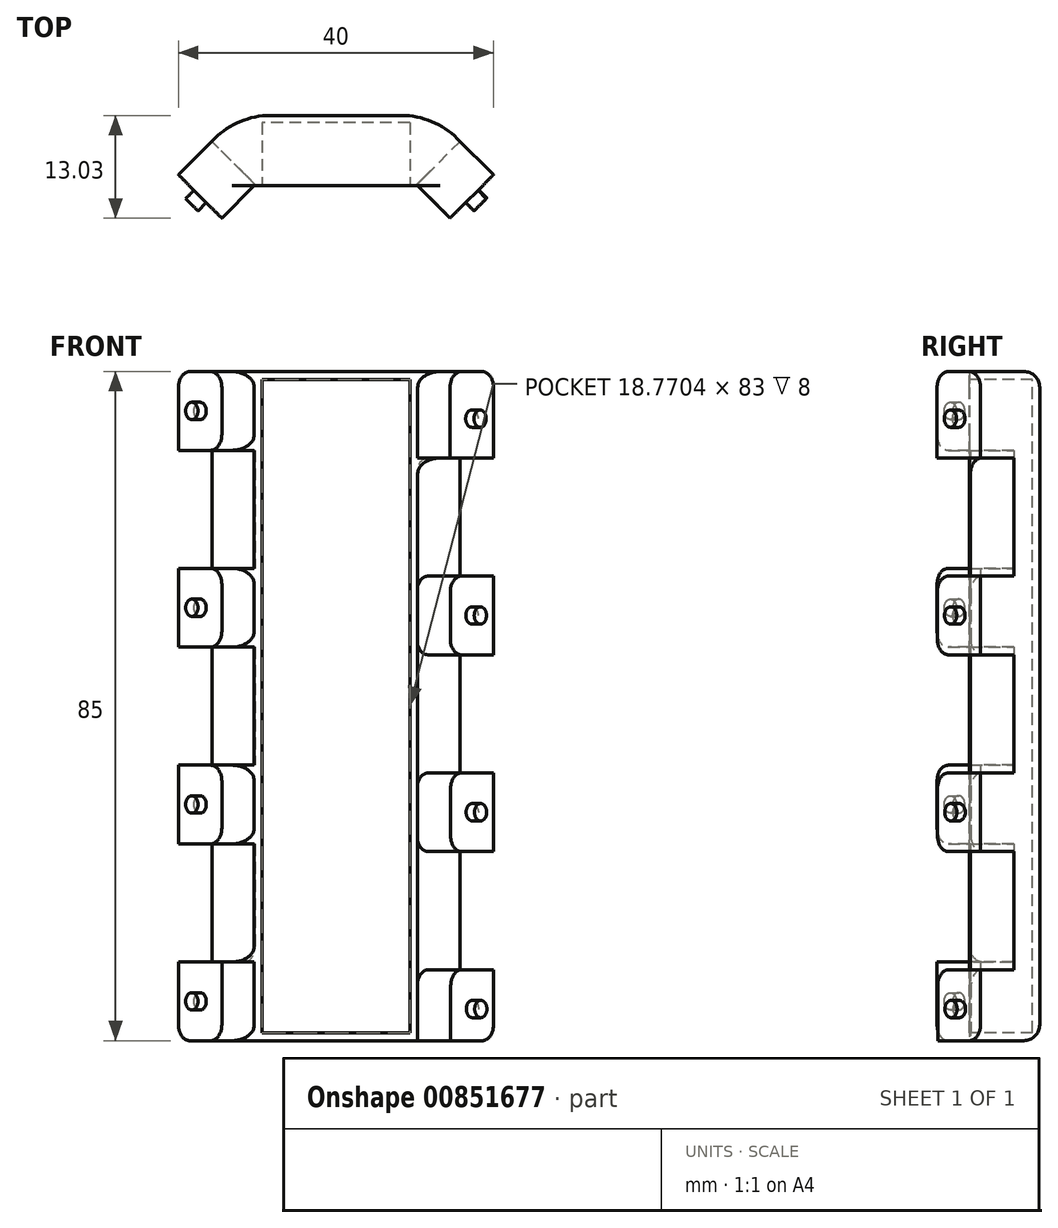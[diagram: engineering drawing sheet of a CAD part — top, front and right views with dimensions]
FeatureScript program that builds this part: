
annotation { "Feature Type Name" : "Feature", "Feature Type Description" : "" }
export const myFeature = defineFeature(function(context is Context, id is Id, definition is map)
    precondition{}
    {
        {
            var Q0;
            Q0=qCreatedBy(makeId("Top.planeOp"),FACE);
            var sketch = newSketch(context, id + "F0", { "sketchPlane" : qUnion([Q0])});
            skLineSegment(sketch, "E0", {"start": v(0, 0) * mm, "end": v(56.57, 56.57) * mm, "construction": true});
            skLineSegment(sketch, "E1", {"start": v(0, 0) * mm, "end": v(-56.57, 56.57) * mm, "construction": true});
            skLineSegment(sketch, "E2", {"start": v(0, 0) * mm, "end": v(14.5, 0) * mm});
            skLineSegment(sketch, "E3", {"start": v(0, 0) * mm, "end": v(-14.5, 0) * mm});
            skLineSegment(sketch, "E4", {"start": v(-14.5, -5.83) * mm, "end": v(-14.5, 16.54) * mm, "construction": true});
            skLineSegment(sketch, "E5", {"start": v(14.5, -3.6) * mm, "end": v(14.5, 17.08) * mm, "construction": true});
            skLineSegment(sketch, "E6", {"start": v(0, 0) * mm, "end": v(-20, 0) * mm, "construction": true});
            skLineSegment(sketch, "E7", {"start": v(0, 0) * mm, "end": v(20, 0) * mm, "construction": true});
            skLineSegment(sketch, "E8", {"start": v(-20, 0) * mm, "end": v(-20, 20) * mm, "construction": true});
            skLineSegment(sketch, "E9", {"start": v(20, 0) * mm, "end": v(20, 20) * mm, "construction": true});
            skLineSegment(sketch, "E10", {"start": v(-14.5, 14.5) * mm, "end": v(-10.39, 18.61) * mm});
            skLineSegment(sketch, "E11", {"start": v(-10.39, 18.61) * mm, "end": v(0, 18.61) * mm});
            skLineSegment(sketch, "E12", {"start": v(-20, 20) * mm, "end": v(-12.47, 27.53) * mm});
            skLineSegment(sketch, "E13", {"start": v(-12.47, 27.53) * mm, "end": v(0, 27.53) * mm});
            skLineSegment(sketch, "E14.MirrorCS", {"start": v(12.47, 27.53) * mm, "end": v(0, 27.53) * mm});
            skLineSegment(sketch, "E15.MirrorCS", {"start": v(20, 20) * mm, "end": v(12.47, 27.53) * mm});
            skLineSegment(sketch, "E16.MirrorCS", {"start": v(14.5, 14.5) * mm, "end": v(10.39, 18.61) * mm});
            skLineSegment(sketch, "E17.MirrorCS", {"start": v(10.39, 18.61) * mm, "end": v(0, 18.61) * mm});
            skLineSegment(sketch, "E18", {"start": v(-20, 20) * mm, "end": v(-14.5, 14.5) * mm});
            skLineSegment(sketch, "E19", {"start": v(14.5, 14.5) * mm, "end": v(20, 20) * mm});
            skSolve(sketch);
        }
        {
            var Q0;
            Q0=makeQuery(id+"F0.imprint","IMPRINT",FACE,{"disambiguationData":[TD([[makeQuery(id+"F0.imprint","IMPRINT",EDGE,{"derivedFrom":sQuery(id+"F0.wireOp",EDGE,"E10")}),1.0]])]});
            extrude(context, id + "F1", {"entities" : qUnion([Q0]), "depth" : 85 * mm, "offsetDistance" : 25 * mm});
        }
        {
            var Q0;
            Q0=makeQuery(id+"F1.opExtrude","SWEPT_EDGE",EDGE,{"disambiguationData":[OSD([sQuery(id+"F0.wireOp",EDGE,"E12"),sQuery(id+"F0.wireOp",EDGE,"E13")])]});
            var Q1;
            Q1=makeQuery(id+"F1.opExtrude","SWEPT_EDGE",EDGE,{"disambiguationData":[OSD([sQuery(id+"F0.wireOp",EDGE,"E14.MirrorCS"),sQuery(id+"F0.wireOp",EDGE,"E15.MirrorCS")])]});
            fillet(context, id + "F2", {"entities" : qUnion([Q0, Q1]), "radius" : 10 * mm, "tangentPropagation" : true, "allowEdgeOverflow" : false});
        }
        {
            var Q0;
            Q0=makeQuery(id+"F1.opExtrude","SWEPT_FACE",FACE,{"disambiguationData":[OSD([sQuery(id+"F0.wireOp",EDGE,"E19")])]});
            var sketch = newSketch(context, id + "F3", { "sketchPlane" : qUnion([Q0])});
            skLineSegment(sketch, "E20.bottom", {"start": v(28.28, 84.02) * mm, "end": v(20.5, 84.02) * mm});
            skLineSegment(sketch, "E20.top", {"start": v(28.28, 74.02) * mm, "end": v(20.5, 74.02) * mm});
            skLineSegment(sketch, "E20.left", {"start": v(28.28, 84.02) * mm, "end": v(28.28, 74.02) * mm});
            skLineSegment(sketch, "E20.right", {"start": v(20.5, 84.02) * mm, "end": v(20.5, 74.02) * mm});
            skLineSegment(sketch, "E21.0.1.0", {"start": v(28.32, 59.02) * mm, "end": v(28.32, 49.02) * mm});
            skLineSegment(sketch, "E21.0.1.1", {"start": v(28.32, 59.02) * mm, "end": v(20.54, 59.02) * mm});
            skLineSegment(sketch, "E21.0.1.2", {"start": v(20.54, 59.02) * mm, "end": v(20.54, 49.02) * mm});
            skLineSegment(sketch, "E21.0.1.3", {"start": v(28.32, 49.02) * mm, "end": v(20.54, 49.02) * mm});
            skLineSegment(sketch, "E21.0.2.0", {"start": v(28.36, 34.02) * mm, "end": v(28.36, 24.02) * mm});
            skLineSegment(sketch, "E21.0.2.1", {"start": v(28.36, 34.02) * mm, "end": v(20.58, 34.02) * mm});
            skLineSegment(sketch, "E21.0.2.2", {"start": v(20.58, 34.02) * mm, "end": v(20.58, 24.02) * mm});
            skLineSegment(sketch, "E21.0.2.3", {"start": v(28.36, 24.02) * mm, "end": v(20.58, 24.02) * mm});
            skLineSegment(sketch, "E21.0.3.0", {"start": v(28.4, 9.02) * mm, "end": v(28.4, -0.98) * mm});
            skLineSegment(sketch, "E21.0.3.1", {"start": v(28.4, 9.02) * mm, "end": v(20.62, 9.02) * mm});
            skLineSegment(sketch, "E21.0.3.2", {"start": v(20.62, 9.02) * mm, "end": v(20.62, -0.98) * mm});
            skLineSegment(sketch, "E21.0.3.3", {"start": v(28.4, -0.98) * mm, "end": v(20.62, -0.98) * mm});
            skLineSegment(sketch, "E21.direction2", {"start": v(28.28, 74.02) * mm, "end": v(28.32, 49.02) * mm, "construction": true});
            skLineSegment(sketch, "E22", {"start": v(24.4, 84.02) * mm, "end": v(24.4, 74.02) * mm, "construction": true});
            skLineSegment(sketch, "E23", {"start": v(28.28, 79.02) * mm, "end": v(20.5, 79.02) * mm, "construction": true});
            skCircle(sketch, "E24", {"center": v(24.4, 79.02) * mm, "radius": 1.1 * mm});
            skLineSegment(sketch, "E25", {"start": v(24.4, 84.02) * mm, "end": v(24.5, -0.98) * mm, "construction": true});
            skCircle(sketch, "E26.1.0.0", {"center": v(24.43, 54.02) * mm, "radius": 1.1 * mm});
            skCircle(sketch, "E26.2.0.0", {"center": v(24.47, 29.02) * mm, "radius": 1.1 * mm});
            skCircle(sketch, "E26.3.0.0", {"center": v(24.51, 4.02) * mm, "radius": 1.1 * mm});
            skLineSegment(sketch, "E26.direction1", {"start": v(24.4, 79.02) * mm, "end": v(24.43, 54.02) * mm, "construction": true});
            skLineSegment(sketch, "E27", {"start": v(28.28, 73.02) * mm, "end": v(20.5, 73.02) * mm, "construction": true});
            skSolve(sketch);
        }
        {
            var Q0;
            {var subQ4=sQuery(id+"F3.wireOp",EDGE,"E20.top");Q0=makeQuery(id+"F3.imprint","IMPRINT",FACE,{"disambiguationData":[TD([[makeQuery(id+"F3.imprint","IMPRINT",EDGE,{"derivedFrom":subQ4}),1.0]])]});}
            extrude(context, id + "F4", {"entities" : qUnion([Q0]), "operationType" : NewBodyOperationType.REMOVE, "oppositeDirection" : true, "depth" : 6 * mm, "offsetDistance" : 25 * mm});
        }
        {
            var Q0;
            Q0=makeQuery(id+"F4.boolean.opBoolean","COPY",EDGE,{"derivedFrom":makeQuery(id+"F4.opExtrude","SWEPT_EDGE",EDGE,{"disambiguationData":[OSD([sQuery(id+"F0.wireOp",EDGE,"E15.MirrorCS"),sQuery(id+"F0.wireOp",EDGE,"E19"),sQuery(id+"F3.wireOp",EDGE,"E20.top"),sQuery(id+"F3.wireOp",EDGE,"E20.left")])]})});
            var Q1;
            Q1=makeQuery(id+"F4.boolean.opBoolean","COPY",EDGE,{"derivedFrom":makeQuery(id+"F4.opExtrude","SWEPT_EDGE",EDGE,{"disambiguationData":[OSD([sQuery(id+"F0.wireOp",EDGE,"E15.MirrorCS"),sQuery(id+"F0.wireOp",EDGE,"E19"),sQuery(id+"F3.wireOp",EDGE,"E21.0.1.3")])]})});
            var Q2;
            Q2=makeQuery(id+"F4.boolean.opBoolean","COPY",EDGE,{"derivedFrom":makeQuery(id+"F4.opExtrude","SWEPT_EDGE",EDGE,{"disambiguationData":[OSD([sQuery(id+"F0.wireOp",EDGE,"E15.MirrorCS"),sQuery(id+"F0.wireOp",EDGE,"E19"),sQuery(id+"F3.wireOp",EDGE,"E21.0.2.3")])]})});
            var Q3;
            Q3=makeQuery(id+"F1.opExtrude","CAP_EDGE",EDGE,{"disambiguationData":[OSD([sQuery(id+"F0.wireOp",EDGE,"E15.MirrorCS")])],"isStart":true});
            var Q4;
            Q4=makeQuery(id+"F4.boolean.opBoolean","COPY",EDGE,{"derivedFrom":makeQuery(id+"F4.opExtrude","SWEPT_EDGE",EDGE,{"disambiguationData":[OSD([sQuery(id+"F0.wireOp",EDGE,"E19"),sQuery(id+"F3.wireOp",EDGE,"E21.0.3.2"),sQuery(id+"F3.wireOp",EDGE,"E21.0.3.3")])]})});
            var Q5;
            Q5=makeQuery(id+"F4.boolean.opBoolean","COPY",EDGE,{"derivedFrom":makeQuery(id+"F4.opExtrude","SWEPT_EDGE",EDGE,{"disambiguationData":[OSD([sQuery(id+"F3.wireOp",EDGE,"E21.0.2.2"),sQuery(id+"F3.wireOp",EDGE,"E21.0.2.3")])]})});
            var Q6;
            Q6=makeQuery(id+"F4.boolean.opBoolean","COPY",EDGE,{"derivedFrom":makeQuery(id+"F4.opExtrude","SWEPT_EDGE",EDGE,{"disambiguationData":[OSD([sQuery(id+"F3.wireOp",EDGE,"E21.0.1.2"),sQuery(id+"F3.wireOp",EDGE,"E21.0.1.3")])]})});
            var Q7;
            {var subQ0=sQuery(id+"F0.wireOp",EDGE,"E16.MirrorCS");var subQ1=sQuery(id+"F3.wireOp",EDGE,"E20.top");Q7=makeQuery(id+"F4.boolean.opBoolean","COPY",EDGE,{"disambiguationData":[topologyDisambiguationEdgeConnected([makeQuery(id+"F1.opExtrude","SWEPT_FACE",FACE,{"disambiguationData":[OSD([subQ0])]})])],"derivedFrom":makeQuery(id+"F4.opExtrude","SWEPT_EDGE",EDGE,{"disambiguationData":[OSD([subQ0,sQuery(id+"F0.wireOp",EDGE,"E19"),subQ1,sQuery(id+"F3.wireOp",EDGE,"E20.right")])]})});}
            var Q8;
            Q8=makeQuery(id+"F1.opExtrude","CAP_EDGE",EDGE,{"disambiguationData":[OSD([sQuery(id+"F0.wireOp",EDGE,"E15.MirrorCS")])],"isStart":false});
            var Q9;
            Q9=makeQuery(id+"F1.opExtrude","CAP_EDGE",EDGE,{"disambiguationData":[OSD([sQuery(id+"F0.wireOp",EDGE,"E16.MirrorCS")])],"isStart":false});
            var Q10;
            Q10=makeQuery(id+"F4.boolean.opBoolean","COPY",EDGE,{"derivedFrom":makeQuery(id+"F4.opExtrude","SWEPT_EDGE",EDGE,{"disambiguationData":[OSD([sQuery(id+"F0.wireOp",EDGE,"E15.MirrorCS"),sQuery(id+"F0.wireOp",EDGE,"E19"),sQuery(id+"F3.wireOp",EDGE,"E21.0.1.1")])]})});
            var Q11;
            Q11=makeQuery(id+"F4.boolean.opBoolean","COPY",EDGE,{"derivedFrom":makeQuery(id+"F4.opExtrude","SWEPT_EDGE",EDGE,{"disambiguationData":[OSD([sQuery(id+"F3.wireOp",EDGE,"E21.0.1.1"),sQuery(id+"F3.wireOp",EDGE,"E21.0.1.2")])]})});
            var Q12;
            Q12=makeQuery(id+"F4.boolean.opBoolean","COPY",EDGE,{"derivedFrom":makeQuery(id+"F4.opExtrude","SWEPT_EDGE",EDGE,{"disambiguationData":[OSD([sQuery(id+"F0.wireOp",EDGE,"E15.MirrorCS"),sQuery(id+"F0.wireOp",EDGE,"E19"),sQuery(id+"F3.wireOp",EDGE,"E21.0.2.1")])]})});
            var Q13;
            Q13=makeQuery(id+"F4.boolean.opBoolean","COPY",EDGE,{"derivedFrom":makeQuery(id+"F4.opExtrude","SWEPT_EDGE",EDGE,{"disambiguationData":[OSD([sQuery(id+"F3.wireOp",EDGE,"E21.0.2.1"),sQuery(id+"F3.wireOp",EDGE,"E21.0.2.2")])]})});
            var Q14;
            Q14=makeQuery(id+"F4.boolean.opBoolean","COPY",EDGE,{"derivedFrom":makeQuery(id+"F4.opExtrude","SWEPT_EDGE",EDGE,{"disambiguationData":[OSD([sQuery(id+"F0.wireOp",EDGE,"E15.MirrorCS"),sQuery(id+"F0.wireOp",EDGE,"E19"),sQuery(id+"F3.wireOp",EDGE,"E21.0.3.1")])]})});
            var Q15;
            Q15=makeQuery(id+"F4.boolean.opBoolean","COPY",EDGE,{"derivedFrom":makeQuery(id+"F4.opExtrude","SWEPT_EDGE",EDGE,{"disambiguationData":[OSD([sQuery(id+"F3.wireOp",EDGE,"E21.0.3.1"),sQuery(id+"F3.wireOp",EDGE,"E21.0.3.2")])]})});
            fillet(context, id + "F5", {"entities" : qUnion([Q0, Q1, Q2, Q3, Q4, Q5, Q6, Q7, Q8, Q9, Q10, Q11, Q12, Q13, Q14, Q15]), "radius" : 2 * mm, "tangentPropagation" : true, "allowEdgeOverflow" : false});
        }
        {
            var Q0;
            Q0=makeQuery(id+"F1.opExtrude","SWEPT_FACE",FACE,{"disambiguationData":[OSD([sQuery(id+"F0.wireOp",EDGE,"E18")])]});
            var sketch = newSketch(context, id + "F6", { "sketchPlane" : qUnion([Q0])});
            skLineSegment(sketch, "E28.bottom", {"start": v(-20.5, 0) * mm, "end": v(-28.28, 0) * mm});
            skLineSegment(sketch, "E28.top", {"start": v(-20.5, 10) * mm, "end": v(-28.28, 10) * mm});
            skLineSegment(sketch, "E28.left", {"start": v(-20.5, 0) * mm, "end": v(-20.5, 10) * mm});
            skLineSegment(sketch, "E28.right", {"start": v(-28.28, 0) * mm, "end": v(-28.28, 10) * mm});
            skLineSegment(sketch, "E29.0.1.0", {"start": v(-20.5, 35) * mm, "end": v(-28.28, 35) * mm});
            skLineSegment(sketch, "E29.0.1.1", {"start": v(-28.28, 25) * mm, "end": v(-28.28, 35) * mm});
            skLineSegment(sketch, "E29.0.1.2", {"start": v(-20.5, 25) * mm, "end": v(-28.28, 25) * mm});
            skLineSegment(sketch, "E29.0.1.3", {"start": v(-20.5, 25) * mm, "end": v(-20.5, 35) * mm});
            skLineSegment(sketch, "E29.0.2.0", {"start": v(-20.5, 60) * mm, "end": v(-28.28, 60) * mm});
            skLineSegment(sketch, "E29.0.2.1", {"start": v(-28.28, 50) * mm, "end": v(-28.28, 60) * mm});
            skLineSegment(sketch, "E29.0.2.2", {"start": v(-20.5, 50) * mm, "end": v(-28.28, 50) * mm});
            skLineSegment(sketch, "E29.0.2.3", {"start": v(-20.5, 50) * mm, "end": v(-20.5, 60) * mm});
            skLineSegment(sketch, "E29.0.3.0", {"start": v(-20.5, 85) * mm, "end": v(-28.28, 85) * mm});
            skLineSegment(sketch, "E29.0.3.1", {"start": v(-28.28, 75) * mm, "end": v(-28.28, 85) * mm});
            skLineSegment(sketch, "E29.0.3.2", {"start": v(-20.5, 75) * mm, "end": v(-28.28, 75) * mm});
            skLineSegment(sketch, "E29.0.3.3", {"start": v(-20.5, 75) * mm, "end": v(-20.5, 85) * mm});
            skLineSegment(sketch, "E29.direction1", {"start": v(-28.28, 10) * mm, "end": v(-3.28, 10) * mm, "construction": true});
            skLineSegment(sketch, "E29.direction2", {"start": v(-28.28, 10) * mm, "end": v(-28.28, 35) * mm, "construction": true});
            skLineSegment(sketch, "E30", {"start": v(-20.5, 5) * mm, "end": v(-30.78, 5) * mm, "construction": true});
            skLineSegment(sketch, "E31", {"start": v(-24.4, 10) * mm, "end": v(-24.4, 0.8) * mm, "construction": true});
            skLineSegment(sketch, "E32.direction1", {"start": v(-24.4, 5) * mm, "end": v(0.6, 5) * mm, "construction": true});
            skLineSegment(sketch, "E32.direction2", {"start": v(-24.4, 5) * mm, "end": v(-24.4, 30) * mm, "construction": true});
            skCircle(sketch, "E33", {"center": v(-24.4, 5) * mm, "radius": 1.1 * mm});
            skCircle(sketch, "E34.0.1.0", {"center": v(-24.4, 30) * mm, "radius": 1.1 * mm});
            skCircle(sketch, "E34.0.2.0", {"center": v(-24.4, 55) * mm, "radius": 1.1 * mm});
            skCircle(sketch, "E34.0.3.0", {"center": v(-24.4, 80) * mm, "radius": 1.1 * mm});
            skSolve(sketch);
        }
        {
            var Q0;
            {var subQ0=sQuery(id+"F6.wireOp",EDGE,"E28.top");Q0=makeQuery(id+"F6.imprint","IMPRINT",FACE,{"disambiguationData":[TD([[makeQuery(id+"F6.imprint","IMPRINT",EDGE,{"derivedFrom":subQ0}),-1.0]])]});}
            var Q1;
            {var subQ0=sQuery(id+"F6.wireOp",EDGE,"E29.0.1.0");Q1=makeQuery(id+"F6.imprint","IMPRINT",FACE,{"disambiguationData":[TD([[makeQuery(id+"F6.imprint","IMPRINT",EDGE,{"derivedFrom":subQ0}),-1.0]])]});}
            var Q2;
            {var subQ0=sQuery(id+"F6.wireOp",EDGE,"E29.0.2.0");Q2=makeQuery(id+"F6.imprint","IMPRINT",FACE,{"disambiguationData":[TD([[makeQuery(id+"F6.imprint","IMPRINT",EDGE,{"derivedFrom":subQ0}),-1.0]])]});}
            extrude(context, id + "F7", {"entities" : qUnion([Q0, Q1, Q2]), "operationType" : NewBodyOperationType.REMOVE, "oppositeDirection" : true, "depth" : 6 * mm, "offsetDistance" : 25 * mm});
        }
        {
            var Q0;
            Q0=makeQuery(id+"F7.boolean.opBoolean","COPY",EDGE,{"derivedFrom":makeQuery(id+"F7.opExtrude","SWEPT_EDGE",EDGE,{"disambiguationData":[OSD([sQuery(id+"F0.wireOp",EDGE,"E12"),sQuery(id+"F0.wireOp",EDGE,"E18"),sQuery(id+"F6.wireOp",EDGE,"E28.top"),sQuery(id+"F6.wireOp",EDGE,"E28.right")])]})});
            var Q1;
            Q1=makeQuery(id+"F7.boolean.opBoolean","COPY",EDGE,{"derivedFrom":makeQuery(id+"F7.opExtrude","SWEPT_EDGE",EDGE,{"disambiguationData":[OSD([sQuery(id+"F0.wireOp",EDGE,"E12"),sQuery(id+"F0.wireOp",EDGE,"E18"),sQuery(id+"F6.wireOp",EDGE,"E29.0.1.1"),sQuery(id+"F6.wireOp",EDGE,"E29.0.1.2")])]})});
            var Q2;
            Q2=makeQuery(id+"F7.boolean.opBoolean","COPY",EDGE,{"derivedFrom":makeQuery(id+"F7.opExtrude","SWEPT_EDGE",EDGE,{"disambiguationData":[OSD([sQuery(id+"F0.wireOp",EDGE,"E12"),sQuery(id+"F0.wireOp",EDGE,"E18"),sQuery(id+"F6.wireOp",EDGE,"E29.0.1.0"),sQuery(id+"F6.wireOp",EDGE,"E29.0.1.1")])]})});
            var Q3;
            Q3=makeQuery(id+"F7.boolean.opBoolean","COPY",EDGE,{"derivedFrom":makeQuery(id+"F7.opExtrude","SWEPT_EDGE",EDGE,{"disambiguationData":[OSD([sQuery(id+"F0.wireOp",EDGE,"E12"),sQuery(id+"F0.wireOp",EDGE,"E18"),sQuery(id+"F6.wireOp",EDGE,"E29.0.2.1"),sQuery(id+"F6.wireOp",EDGE,"E29.0.2.2")])]})});
            var Q4;
            Q4=makeQuery(id+"F7.boolean.opBoolean","COPY",EDGE,{"derivedFrom":makeQuery(id+"F7.opExtrude","SWEPT_EDGE",EDGE,{"disambiguationData":[OSD([sQuery(id+"F0.wireOp",EDGE,"E12"),sQuery(id+"F0.wireOp",EDGE,"E18"),sQuery(id+"F6.wireOp",EDGE,"E29.0.2.0"),sQuery(id+"F6.wireOp",EDGE,"E29.0.2.1")])]})});
            var Q5;
            Q5=makeQuery(id+"F7.boolean.opBoolean","COPY",EDGE,{"derivedFrom":makeQuery(id+"F7.opExtrude","SWEPT_EDGE",EDGE,{"disambiguationData":[OSD([sQuery(id+"F0.wireOp",EDGE,"E12"),sQuery(id+"F0.wireOp",EDGE,"E18"),sQuery(id+"F6.wireOp",EDGE,"E29.0.3.1"),sQuery(id+"F6.wireOp",EDGE,"E29.0.3.2")])]})});
            var Q6;
            Q6=makeQuery(id+"F1.opExtrude","CAP_EDGE",EDGE,{"disambiguationData":[OSD([sQuery(id+"F0.wireOp",EDGE,"E10")])],"isStart":false});
            var Q7;
            {var subQ0=sQuery(id+"F0.wireOp",EDGE,"E10");var subQ1=sQuery(id+"F6.wireOp",EDGE,"E29.0.3.2");Q7=makeQuery(id+"F7.boolean.opBoolean","COPY",EDGE,{"disambiguationData":[topologyDisambiguationEdgeConnected([makeQuery(id+"F1.opExtrude","SWEPT_FACE",FACE,{"disambiguationData":[OSD([subQ0])]})])],"derivedFrom":makeQuery(id+"F7.opExtrude","SWEPT_EDGE",EDGE,{"disambiguationData":[OSD([subQ0,sQuery(id+"F0.wireOp",EDGE,"E18"),subQ1,sQuery(id+"F6.wireOp",EDGE,"E29.0.3.3")])]})});}
            var Q8;
            {var subQ0=sQuery(id+"F0.wireOp",EDGE,"E10");var subQ1=sQuery(id+"F6.wireOp",EDGE,"E29.0.2.0");Q8=makeQuery(id+"F7.boolean.opBoolean","COPY",EDGE,{"disambiguationData":[topologyDisambiguationEdgeConnected([makeQuery(id+"F1.opExtrude","SWEPT_FACE",FACE,{"disambiguationData":[OSD([subQ0])]})])],"derivedFrom":makeQuery(id+"F7.opExtrude","SWEPT_EDGE",EDGE,{"disambiguationData":[OSD([subQ0,sQuery(id+"F0.wireOp",EDGE,"E18"),subQ1,sQuery(id+"F6.wireOp",EDGE,"E29.0.2.3")])]})});}
            var Q9;
            {var subQ0=sQuery(id+"F0.wireOp",EDGE,"E10");var subQ1=sQuery(id+"F6.wireOp",EDGE,"E29.0.2.2");Q9=makeQuery(id+"F7.boolean.opBoolean","COPY",EDGE,{"disambiguationData":[topologyDisambiguationEdgeConnected([makeQuery(id+"F1.opExtrude","SWEPT_FACE",FACE,{"disambiguationData":[OSD([subQ0])]})])],"derivedFrom":makeQuery(id+"F7.opExtrude","SWEPT_EDGE",EDGE,{"disambiguationData":[OSD([subQ0,sQuery(id+"F0.wireOp",EDGE,"E18"),subQ1,sQuery(id+"F6.wireOp",EDGE,"E29.0.2.3")])]})});}
            var Q10;
            {var subQ0=sQuery(id+"F0.wireOp",EDGE,"E10");var subQ1=sQuery(id+"F6.wireOp",EDGE,"E29.0.1.0");Q10=makeQuery(id+"F7.boolean.opBoolean","COPY",EDGE,{"disambiguationData":[topologyDisambiguationEdgeConnected([makeQuery(id+"F1.opExtrude","SWEPT_FACE",FACE,{"disambiguationData":[OSD([subQ0])]})])],"derivedFrom":makeQuery(id+"F7.opExtrude","SWEPT_EDGE",EDGE,{"disambiguationData":[OSD([subQ0,sQuery(id+"F0.wireOp",EDGE,"E18"),subQ1,sQuery(id+"F6.wireOp",EDGE,"E29.0.1.3")])]})});}
            var Q11;
            {var subQ0=sQuery(id+"F0.wireOp",EDGE,"E10");var subQ1=sQuery(id+"F6.wireOp",EDGE,"E29.0.1.2");Q11=makeQuery(id+"F7.boolean.opBoolean","COPY",EDGE,{"disambiguationData":[topologyDisambiguationEdgeConnected([makeQuery(id+"F1.opExtrude","SWEPT_FACE",FACE,{"disambiguationData":[OSD([subQ0])]})])],"derivedFrom":makeQuery(id+"F7.opExtrude","SWEPT_EDGE",EDGE,{"disambiguationData":[OSD([subQ0,sQuery(id+"F0.wireOp",EDGE,"E18"),subQ1,sQuery(id+"F6.wireOp",EDGE,"E29.0.1.3")])]})});}
            var Q12;
            {var subQ0=sQuery(id+"F0.wireOp",EDGE,"E10");var subQ1=sQuery(id+"F6.wireOp",EDGE,"E28.top");Q12=makeQuery(id+"F7.boolean.opBoolean","COPY",EDGE,{"disambiguationData":[topologyDisambiguationEdgeConnected([makeQuery(id+"F1.opExtrude","SWEPT_FACE",FACE,{"disambiguationData":[OSD([subQ0])]})])],"derivedFrom":makeQuery(id+"F7.opExtrude","SWEPT_EDGE",EDGE,{"disambiguationData":[OSD([subQ0,sQuery(id+"F0.wireOp",EDGE,"E18"),subQ1,sQuery(id+"F6.wireOp",EDGE,"E28.left")])]})});}
            var Q13;
            Q13=makeQuery(id+"F1.opExtrude","CAP_EDGE",EDGE,{"disambiguationData":[OSD([sQuery(id+"F0.wireOp",EDGE,"E10")])],"isStart":true});
            fillet(context, id + "F8", {"entities" : qUnion([Q0, Q1, Q2, Q3, Q4, Q5, Q6, Q7, Q8, Q9, Q10, Q11, Q12, Q13]), "radius" : 2 * mm, "tangentPropagation" : true, "allowEdgeOverflow" : false});
        }
        {
            var Q0;
            Q0=makeQuery(id+"F6.imprint","IMPRINT",FACE,{"disambiguationData":[TD([[makeQuery(id+"F6.imprint","IMPRINT",EDGE,{"derivedFrom":sQuery(id+"F6.wireOp",EDGE,"E33")}),1.0]])]});
            var Q1;
            Q1=makeQuery(id+"F6.imprint","IMPRINT",FACE,{"disambiguationData":[TD([[makeQuery(id+"F6.imprint","IMPRINT",EDGE,{"derivedFrom":sQuery(id+"F6.wireOp",EDGE,"E34.0.1.0")}),1.0]])]});
            var Q2;
            Q2=makeQuery(id+"F6.imprint","IMPRINT",FACE,{"disambiguationData":[TD([[makeQuery(id+"F6.imprint","IMPRINT",EDGE,{"derivedFrom":sQuery(id+"F6.wireOp",EDGE,"E34.0.2.0")}),1.0]])]});
            var Q3;
            Q3=makeQuery(id+"F6.imprint","IMPRINT",FACE,{"disambiguationData":[TD([[makeQuery(id+"F6.imprint","IMPRINT",EDGE,{"derivedFrom":sQuery(id+"F6.wireOp",EDGE,"E34.0.3.0")}),1.0]])]});
            extrude(context, id + "F9", {"entities" : qUnion([Q0, Q1, Q2, Q3]), "operationType" : NewBodyOperationType.ADD, "depth" : 1.5 * mm, "offsetDistance" : 25 * mm});
        }
        {
            var Q0;
            Q0=makeQuery(id+"F3.imprint","IMPRINT",FACE,{"disambiguationData":[TD([[makeQuery(id+"F3.imprint","IMPRINT",EDGE,{"derivedFrom":sQuery(id+"F3.wireOp",EDGE,"E24")}),1.0]])]});
            var Q1;
            Q1=makeQuery(id+"F3.imprint","IMPRINT",FACE,{"disambiguationData":[TD([[makeQuery(id+"F3.imprint","IMPRINT",EDGE,{"derivedFrom":sQuery(id+"F3.wireOp",EDGE,"E26.1.0.0")}),1.0]])]});
            var Q2;
            Q2=makeQuery(id+"F3.imprint","IMPRINT",FACE,{"disambiguationData":[TD([[makeQuery(id+"F3.imprint","IMPRINT",EDGE,{"derivedFrom":sQuery(id+"F3.wireOp",EDGE,"E26.2.0.0")}),1.0]])]});
            var Q3;
            Q3=makeQuery(id+"F3.imprint","IMPRINT",FACE,{"disambiguationData":[TD([[makeQuery(id+"F3.imprint","IMPRINT",EDGE,{"derivedFrom":sQuery(id+"F3.wireOp",EDGE,"E26.3.0.0")}),1.0]])]});
            extrude(context, id + "F10", {"entities" : qUnion([Q0, Q1, Q2, Q3]), "operationType" : NewBodyOperationType.ADD, "depth" : 1.5 * mm, "offsetDistance" : 25 * mm});
        }
        {
            var Q0;
            Q0=makeQuery(id+"F1.opExtrude","SWEPT_FACE",FACE,{"disambiguationData":[OSD([sQuery(id+"F0.wireOp",EDGE,"E11"),sQuery(id+"F0.wireOp",EDGE,"E17.MirrorCS")])]});
            var sketch = newSketch(context, id + "F11", { "sketchPlane" : qUnion([Q0])});
            skLineSegment(sketch, "E35.bottom", {"start": v(9.39, 1) * mm, "end": v(-9.39, 1) * mm});
            skLineSegment(sketch, "E35.top", {"start": v(9.39, 84) * mm, "end": v(-9.39, 84) * mm});
            skLineSegment(sketch, "E35.left", {"start": v(9.39, 1) * mm, "end": v(9.39, 84) * mm});
            skLineSegment(sketch, "E35.right", {"start": v(-9.39, 1) * mm, "end": v(-9.39, 84) * mm});
            skSolve(sketch);
        }
        {
            var Q0;
            Q0=makeQuery(id+"F11.imprint","IMPRINT",FACE,{"disambiguationData":[TD([[makeQuery(id+"F11.imprint","IMPRINT",EDGE,{"derivedFrom":sQuery(id+"F11.wireOp",EDGE,"E35.bottom")}),-1.0]])]});
            extrude(context, id + "F12", {"entities" : qUnion([Q0]), "operationType" : NewBodyOperationType.REMOVE, "oppositeDirection" : true, "depth" : 8 * mm, "offsetDistance" : 25 * mm});
        }
    });
